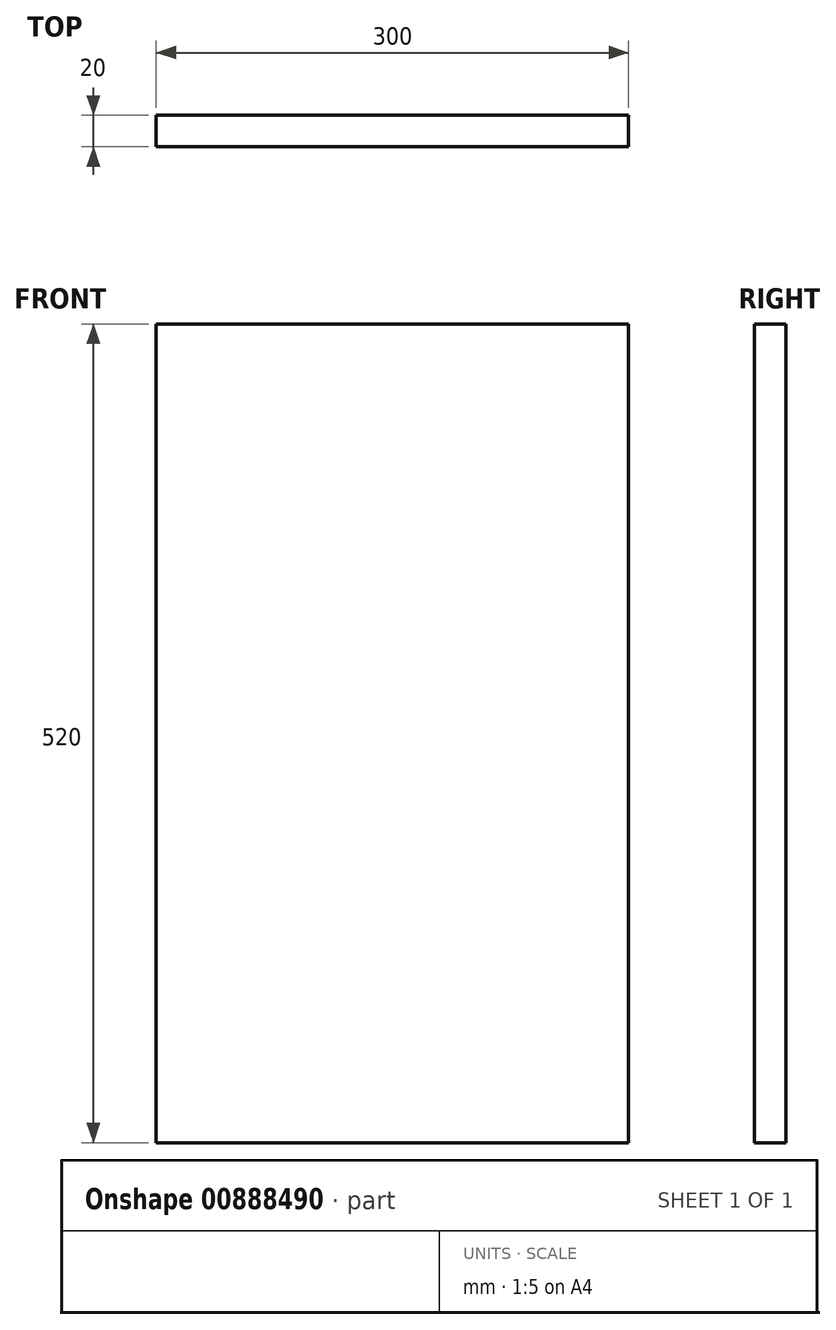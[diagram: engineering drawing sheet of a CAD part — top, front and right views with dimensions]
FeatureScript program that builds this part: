
annotation { "Feature Type Name" : "Feature", "Feature Type Description" : "" }
export const myFeature = defineFeature(function(context is Context, id is Id, definition is map)
    precondition{}
    {
        {
            var Q0;
            Q0=qCreatedBy(makeId("Front.planeOp"),FACE);
            var sketch = newSketch(context, id + "F0", { "sketchPlane" : qUnion([Q0])});
            skLineSegment(sketch, "E0.bottom", {"start": v(150, 260) * mm, "end": v(-150, 260) * mm});
            skLineSegment(sketch, "E0.top", {"start": v(150, -260) * mm, "end": v(-150, -260) * mm});
            skLineSegment(sketch, "E0.left", {"start": v(150, 260) * mm, "end": v(150, -260) * mm});
            skLineSegment(sketch, "E0.right", {"start": v(-150, 260) * mm, "end": v(-150, -260) * mm});
            skPoint(sketch, "E0.middle", {"position": v(0, 0) * mm});
            skSolve(sketch);
        }
        {
            var Q0;
            Q0 = qSketchRegion(id + "F0", true);
            extrude(context, id + "F1", {"entities" : qUnion([Q0]), "depth" : 20 * mm, "offsetDistance" : 25 * mm});
        }
    });
